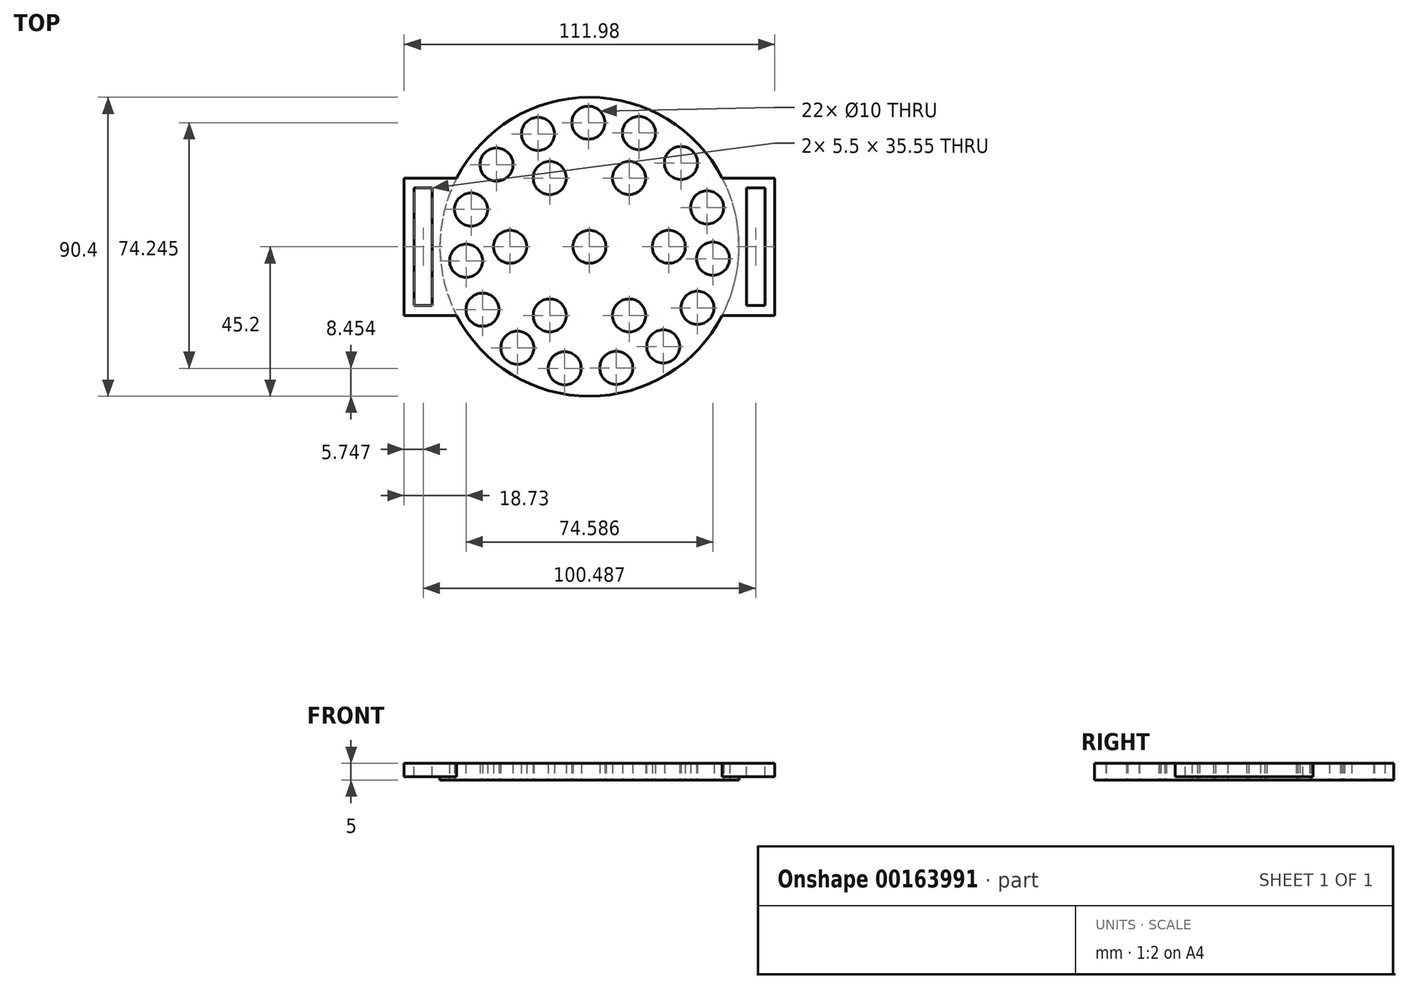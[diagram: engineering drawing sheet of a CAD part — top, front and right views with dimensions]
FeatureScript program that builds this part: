
annotation { "Feature Type Name" : "Feature", "Feature Type Description" : "" }
export const myFeature = defineFeature(function(context is Context, id is Id, definition is map)
    precondition{}
    {
        {
            var Q0;
            Q0=qCreatedBy(makeId("Top.planeOp"),FACE);
            var sketch = newSketch(context, id + "F0", { "sketchPlane" : qUnion([Q0])});
            skCircle(sketch, "E0", {"center": v(0, 0) * mm, "radius": 37.5 * mm});
            skCircle(sketch, "E1.cCircle", {"center": v(0, 0) * mm, "radius": 37.5 * mm, "construction": true});
            skLineSegment(sketch, "E1.0", {"start": v(-28.08, 24.85) * mm, "end": v(-15.55, 34.13) * mm, "construction": true});
            skLineSegment(sketch, "E1.1", {"start": v(-15.55, 34.13) * mm, "end": v(-0.32, 37.5) * mm, "construction": true});
            skLineSegment(sketch, "E1.2", {"start": v(-0.32, 37.5) * mm, "end": v(14.96, 34.39) * mm, "construction": true});
            skLineSegment(sketch, "E1.3", {"start": v(14.96, 34.39) * mm, "end": v(27.65, 25.33) * mm, "construction": true});
            skLineSegment(sketch, "E1.4", {"start": v(27.65, 25.33) * mm, "end": v(35.56, 11.9) * mm, "construction": true});
            skLineSegment(sketch, "E1.5", {"start": v(35.56, 11.9) * mm, "end": v(37.33, -3.6) * mm, "construction": true});
            skLineSegment(sketch, "E1.6", {"start": v(37.33, -3.6) * mm, "end": v(32.64, -18.47) * mm, "construction": true});
            skLineSegment(sketch, "E1.7", {"start": v(32.64, -18.47) * mm, "end": v(22.3, -30.15) * mm, "construction": true});
            skLineSegment(sketch, "E1.8", {"start": v(22.3, -30.15) * mm, "end": v(8.11, -36.61) * mm, "construction": true});
            skLineSegment(sketch, "E1.9", {"start": v(8.11, -36.61) * mm, "end": v(-7.48, -36.75) * mm, "construction": true});
            skLineSegment(sketch, "E1.10", {"start": v(-7.48, -36.75) * mm, "end": v(-21.78, -30.53) * mm, "construction": true});
            skLineSegment(sketch, "E1.11", {"start": v(-21.78, -30.53) * mm, "end": v(-32.31, -19.03) * mm, "construction": true});
            skLineSegment(sketch, "E1.12", {"start": v(-32.31, -19.03) * mm, "end": v(-37.26, -4.24) * mm, "construction": true});
            skLineSegment(sketch, "E1.13", {"start": v(-37.26, -4.24) * mm, "end": v(-35.76, 11.28) * mm, "construction": true});
            skLineSegment(sketch, "E1.14", {"start": v(-35.76, 11.28) * mm, "end": v(-28.08, 24.85) * mm, "construction": true});
            skCircle(sketch, "E2", {"center": v(0, 0) * mm, "radius": 45.2 * mm});
            skCircle(sketch, "E3", {"center": v(-28.08, 24.85) * mm, "radius": 5 * mm});
            skCircle(sketch, "E4", {"center": v(-15.55, 34.13) * mm, "radius": 5 * mm});
            skCircle(sketch, "E5", {"center": v(-0.32, 37.5) * mm, "radius": 5 * mm});
            skCircle(sketch, "E6", {"center": v(14.96, 34.39) * mm, "radius": 5 * mm});
            skCircle(sketch, "E7", {"center": v(27.65, 25.33) * mm, "radius": 5 * mm});
            skCircle(sketch, "E8", {"center": v(35.56, 11.9) * mm, "radius": 5 * mm});
            skCircle(sketch, "E9", {"center": v(37.33, -3.6) * mm, "radius": 5 * mm});
            skCircle(sketch, "E10", {"center": v(32.64, -18.47) * mm, "radius": 5 * mm});
            skCircle(sketch, "E11", {"center": v(22.3, -30.15) * mm, "radius": 5 * mm});
            skCircle(sketch, "E12", {"center": v(8.11, -36.61) * mm, "radius": 5 * mm});
            skCircle(sketch, "E13", {"center": v(-7.48, -36.75) * mm, "radius": 5 * mm});
            skCircle(sketch, "E14", {"center": v(-21.78, -30.53) * mm, "radius": 5 * mm});
            skCircle(sketch, "E15", {"center": v(-32.31, -19.03) * mm, "radius": 5 * mm});
            skCircle(sketch, "E16", {"center": v(-37.26, -4.24) * mm, "radius": 5 * mm});
            skCircle(sketch, "E17", {"center": v(-35.76, 11.28) * mm, "radius": 5 * mm});
            skCircle(sketch, "E18.cCircle", {"center": v(0, 0) * mm, "radius": 23.99 * mm, "construction": true});
            skLineSegment(sketch, "E18.0", {"start": v(-12, 20.77) * mm, "end": v(12, 20.77) * mm});
            skLineSegment(sketch, "E18.1", {"start": v(12, 20.77) * mm, "end": v(23.99, 0) * mm});
            skLineSegment(sketch, "E18.2", {"start": v(23.99, 0) * mm, "end": v(12, -20.77) * mm});
            skLineSegment(sketch, "E18.3", {"start": v(12, -20.77) * mm, "end": v(-12, -20.77) * mm});
            skLineSegment(sketch, "E18.4", {"start": v(-12, -20.77) * mm, "end": v(-23.99, 0) * mm});
            skLineSegment(sketch, "E18.5", {"start": v(-23.99, 0) * mm, "end": v(-12, 20.77) * mm});
            skCircle(sketch, "E19", {"center": v(-12, 20.77) * mm, "radius": 5 * mm});
            skCircle(sketch, "E20", {"center": v(12, 20.77) * mm, "radius": 5 * mm});
            skCircle(sketch, "E21", {"center": v(23.99, 0) * mm, "radius": 5 * mm});
            skCircle(sketch, "E22", {"center": v(12, -20.77) * mm, "radius": 5 * mm});
            skCircle(sketch, "E23", {"center": v(-12, -20.77) * mm, "radius": 5 * mm});
            skCircle(sketch, "E24", {"center": v(-23.99, 0) * mm, "radius": 5 * mm});
            skCircle(sketch, "E25", {"center": v(0, 0) * mm, "radius": 5 * mm});
            skSolve(sketch);
        }
        {
            var Q0;
            {var subQ1=sQuery(id+"F0.wireOp",EDGE,"E0");var subQ4=sQuery(id+"F0.wireOp",EDGE,"E8");var subQ5=makeQuery(id+"F0.imprint","INTERSECT",VERTEX,{"disambiguationData":[OD(0.0)],"derivedFrom":[subQ1,subQ4]});Q0=makeQuery(id+"F0.imprint","IMPRINT",FACE,{"disambiguationData":[TD([[makeQuery(id+"F0.imprint","IMPRINT",EDGE,{"disambiguationData":[TD([[subQ5,1.0]])],"derivedFrom":subQ1}),1.0]])]});}
            var Q1;
            Q1=makeQuery(id+"F0.imprint","IMPRINT",FACE,{"disambiguationData":[TD([[makeQuery(id+"F0.imprint","IMPRINT",EDGE,{"derivedFrom":sQuery(id+"F0.wireOp",EDGE,"E2")}),1.0]])]});
            var Q2;
            Q2=makeQuery(id+"F0.imprint","IMPRINT",FACE,{"disambiguationData":[TD([[makeQuery(id+"F0.imprint","IMPRINT",EDGE,{"derivedFrom":sQuery(id+"F0.wireOp",EDGE,"E25")}),-1.0]])]});
            extrude(context, id + "F1", {"entities" : qUnion([Q0, Q1, Q2]), "depth" : 5 * mm});
        }
        {
            var Q0;
            Q0=makeQuery(id+"F1.opExtrude","CAP_FACE",FACE,{"disambiguationData":[OSD([sQuery(id+"F0.wireOp",EDGE,"E2"),sQuery(id+"F0.wireOp",EDGE,"E3"),sQuery(id+"F0.wireOp",EDGE,"E4"),sQuery(id+"F0.wireOp",EDGE,"E5"),sQuery(id+"F0.wireOp",EDGE,"E6"),sQuery(id+"F0.wireOp",EDGE,"E7"),sQuery(id+"F0.wireOp",EDGE,"E8"),sQuery(id+"F0.wireOp",EDGE,"E9"),sQuery(id+"F0.wireOp",EDGE,"E10"),sQuery(id+"F0.wireOp",EDGE,"E11"),sQuery(id+"F0.wireOp",EDGE,"E12"),sQuery(id+"F0.wireOp",EDGE,"E13"),sQuery(id+"F0.wireOp",EDGE,"E14"),sQuery(id+"F0.wireOp",EDGE,"E15"),sQuery(id+"F0.wireOp",EDGE,"E16"),sQuery(id+"F0.wireOp",EDGE,"E17"),sQuery(id+"F0.wireOp",EDGE,"E19"),sQuery(id+"F0.wireOp",EDGE,"E20"),sQuery(id+"F0.wireOp",EDGE,"E21"),sQuery(id+"F0.wireOp",EDGE,"E22"),sQuery(id+"F0.wireOp",EDGE,"E23"),sQuery(id+"F0.wireOp",EDGE,"E24"),sQuery(id+"F0.wireOp",EDGE,"E25")])],"isStart":false});
            var sketch = newSketch(context, id + "F2", { "sketchPlane" : qUnion([Q0])});
            skCircle(sketch, "E26.0", {"center": v(0, 0) * mm, "radius": 45.2 * mm});
            skCircle(sketch, "E27.0", {"center": v(-12, 20.77) * mm, "radius": 5 * mm});
            skCircle(sketch, "E27.1", {"center": v(-12, -20.77) * mm, "radius": 5 * mm});
            skCircle(sketch, "E27.2", {"center": v(12, -20.77) * mm, "radius": 5 * mm});
            skCircle(sketch, "E27.3", {"center": v(12, 20.77) * mm, "radius": 5 * mm});
            skLineSegment(sketch, "E28", {"start": v(-56, 20.77) * mm, "end": v(-56, -20.77) * mm});
            skLineSegment(sketch, "E29", {"start": v(-56, -20.77) * mm, "end": v(-40.15, -20.77) * mm});
            skLineSegment(sketch, "E30", {"start": v(56, 20.77) * mm, "end": v(56, -20.77) * mm});
            skLineSegment(sketch, "E31", {"start": v(40.15, -20.77) * mm, "end": v(56, -20.77) * mm});
            skLineSegment(sketch, "E32.0", {"start": v(-53, -17.77) * mm, "end": v(-47.5, -17.77) * mm});
            skLineSegment(sketch, "E32.1", {"start": v(-53, 17.77) * mm, "end": v(-53, -17.77) * mm});
            skLineSegment(sketch, "E33.1", {"start": v(53, 17.77) * mm, "end": v(53, -17.77) * mm});
            skLineSegment(sketch, "E34", {"start": v(47.5, 17.77) * mm, "end": v(47.5, -17.77) * mm});
            skLineSegment(sketch, "E35", {"start": v(-47.5, 17.77) * mm, "end": v(-47.5, -17.77) * mm});
            skLineSegment(sketch, "E36", {"start": v(47.5, 17.77) * mm, "end": v(53, 17.77) * mm});
            skLineSegment(sketch, "E37.trimOffspring", {"start": v(-47.5, 17.77) * mm, "end": v(-53, 17.77) * mm});
            skLineSegment(sketch, "E38.trimOffspring", {"start": v(-40.15, 20.77) * mm, "end": v(-56, 20.77) * mm});
            skLineSegment(sketch, "E39.trimOffspring", {"start": v(40.15, 20.77) * mm, "end": v(56, 20.77) * mm});
            skLineSegment(sketch, "E40.trimOffspring", {"start": v(47.5, -17.77) * mm, "end": v(53, -17.77) * mm});
            skSolve(sketch);
        }
        {
            var Q0;
            Q0=makeQuery(id+"F2.imprint","IMPRINT",FACE,{"disambiguationData":[TD([[makeQuery(id+"F2.imprint","IMPRINT",EDGE,{"derivedFrom":sQuery(id+"F2.wireOp",EDGE,"E28")}),1.0]])]});
            var Q1;
            Q1=makeQuery(id+"F2.imprint","IMPRINT",FACE,{"disambiguationData":[TD([[makeQuery(id+"F2.imprint","IMPRINT",EDGE,{"derivedFrom":sQuery(id+"F2.wireOp",EDGE,"E30")}),-1.0]])]});
            extrude(context, id + "F3", {"entities" : qUnion([Q0, Q1]), "operationType" : NewBodyOperationType.ADD, "oppositeDirection" : true, "depth" : 4 * mm});
        }
    });
